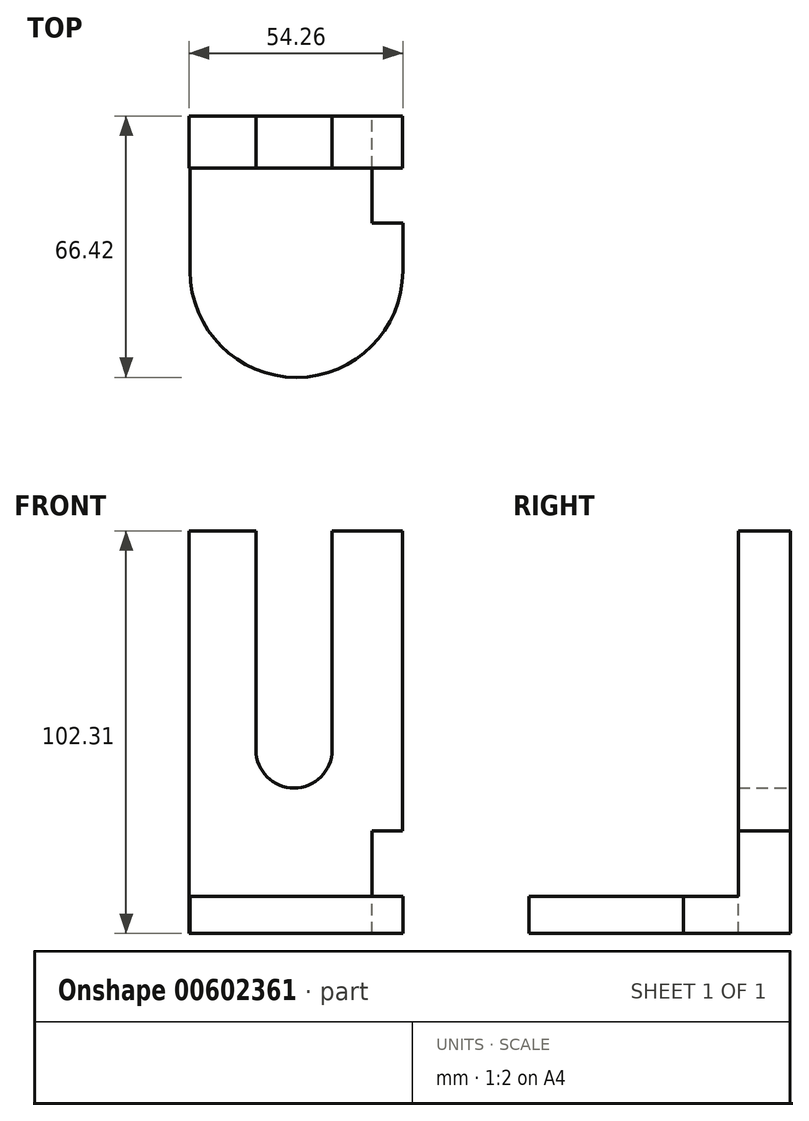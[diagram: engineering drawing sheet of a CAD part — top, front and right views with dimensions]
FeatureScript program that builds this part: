
annotation { "Feature Type Name" : "Feature", "Feature Type Description" : "" }
export const myFeature = defineFeature(function(context is Context, id is Id, definition is map)
    precondition{}
    {
        {
            var Q0;
            Q0=qCreatedBy(makeId("Front.planeOp"),FACE);
            var sketch = newSketch(context, id + "F0", { "sketchPlane" : qUnion([Q0])});
            skLineSegment(sketch, "E0.bottom", {"start": v(-27.16, 55.64) * mm, "end": v(27.07, 55.64) * mm});
            skLineSegment(sketch, "E0.top", {"start": v(-27.16, -46.67) * mm, "end": v(27.07, -46.67) * mm});
            skLineSegment(sketch, "E0.left", {"start": v(-27.16, 55.64) * mm, "end": v(-27.16, -46.67) * mm});
            skLineSegment(sketch, "E0.right", {"start": v(27.07, 55.64) * mm, "end": v(27.07, -46.67) * mm});
            skSolve(sketch);
        }
        {
            var Q0;
            Q0=makeQuery(id+"F0.imprint","IMPRINT",FACE,{"disambiguationData":[TD([[makeQuery(id+"F0.imprint","IMPRINT",EDGE,{"derivedFrom":sQuery(id+"F0.wireOp",EDGE,"E0.bottom")}),-1.0]])]});
            extrude(context, id + "F1", {"entities" : qUnion([Q0]), "depth" : 13.2 * mm, "offsetDistance" : 25.4 * mm});
        }
        {
            var Q0;
            Q0=qCreatedBy(makeId("Front.planeOp"),FACE);
            var sketch = newSketch(context, id + "F2", { "sketchPlane" : qUnion([Q0])});
            skLineSegment(sketch, "E1.bottom", {"start": v(-10.22, 55.7) * mm, "end": v(9.14, 55.7) * mm});
            skLineSegment(sketch, "E1.top", {"start": v(-10.22, 0) * mm, "end": v(9.14, 0) * mm});
            skLineSegment(sketch, "E1.left", {"start": v(-10.22, 55.7) * mm, "end": v(-10.22, 0) * mm});
            skLineSegment(sketch, "E1.right", {"start": v(9.14, 55.7) * mm, "end": v(9.14, 0) * mm});
            skArc(sketch, "E2", {"start": v(-10.22, 0) * mm, "mid": v(-0.54, -9.68) * mm, "end": v(9.14, 0) * mm});
            skSolve(sketch);
        }
        {
            var Q0;
            Q0 = qSketchRegion(id + "F2", true);
            extrude(context, id + "F3", {"entities" : qUnion([Q0]), "operationType" : NewBodyOperationType.REMOVE, "depth" : 42.16 * mm, "offsetDistance" : 25.4 * mm});
        }
        {
            var Q0;
            Q0=qCreatedBy(makeId("Front.planeOp"),FACE);
            var sketch = newSketch(context, id + "F4", { "sketchPlane" : qUnion([Q0])});
            skLineSegment(sketch, "E3.bottom", {"start": v(19.25, -50.33) * mm, "end": v(34.52, -50.33) * mm});
            skLineSegment(sketch, "E3.top", {"start": v(19.25, -20.65) * mm, "end": v(34.52, -20.65) * mm});
            skLineSegment(sketch, "E3.left", {"start": v(19.25, -50.33) * mm, "end": v(19.25, -20.65) * mm});
            skLineSegment(sketch, "E3.right", {"start": v(34.52, -50.33) * mm, "end": v(34.52, -20.65) * mm});
            skSolve(sketch);
        }
        {
            var Q0;
            Q0=makeQuery(id+"F1.opExtrude","SWEPT_FACE",FACE,{"disambiguationData":[OSD([sQuery(id+"F0.wireOp",EDGE,"E0.top")])]});
            cPlane(context, id + "F5", {"entities" : qUnion([Q0]), "cplaneType" : CPlaneType.OFFSET, "offset" : 0 * mm, "width" : 152.4 * mm, "height" : 152.4 * mm});
        }
        {
            var Q0;
            Q0=qCreatedBy(id+"F5.planeOp",FACE);
            var sketch = newSketch(context, id + "F6", { "sketchPlane" : qUnion([Q0])});
            skLineSegment(sketch, "E4.bottom", {"start": v(-26.94, 0) * mm, "end": v(27.1, 0) * mm});
            skLineSegment(sketch, "E4.top", {"start": v(-26.94, 39.4) * mm, "end": v(27.1, 39.4) * mm});
            skLineSegment(sketch, "E4.left", {"start": v(-26.94, 0) * mm, "end": v(-26.94, 39.4) * mm});
            skLineSegment(sketch, "E4.right", {"start": v(27.1, 0) * mm, "end": v(27.1, 39.4) * mm});
            skArc(sketch, "E5", {"start": v(27.1, 39.4) * mm, "mid": v(0.08, 66.42) * mm, "end": v(-26.94, 39.4) * mm});
            skSolve(sketch);
        }
        {
            var Q0;
            Q0 = qSketchRegion(id + "F6", true);
            extrude(context, id + "F7", {"entities" : qUnion([Q0]), "operationType" : NewBodyOperationType.ADD, "oppositeDirection" : true, "depth" : 9.4 * mm, "offsetDistance" : 25.4 * mm});
        }
        {
            var Q0;
            Q0=makeQuery(id+"F4.imprint","IMPRINT",FACE,{"disambiguationData":[TD([[makeQuery(id+"F4.imprint","IMPRINT",EDGE,{"derivedFrom":sQuery(id+"F4.wireOp",EDGE,"E3.bottom")}),1.0]])]});
            extrude(context, id + "F8", {"entities" : qUnion([Q0]), "operationType" : NewBodyOperationType.REMOVE, "depth" : 27.18 * mm, "offsetDistance" : 25.4 * mm});
        }
    });
